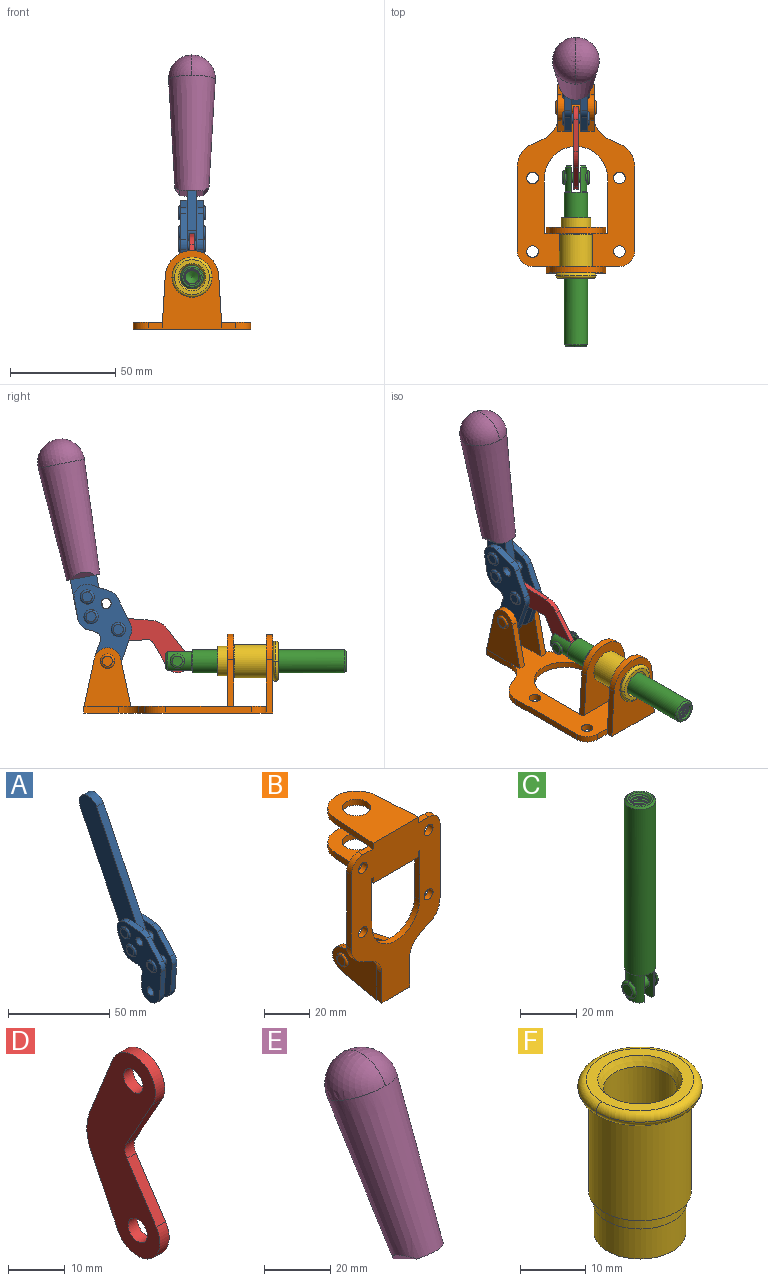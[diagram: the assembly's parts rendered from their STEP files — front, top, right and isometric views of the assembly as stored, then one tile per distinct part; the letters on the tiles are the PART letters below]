
ASSEMBLY  parts=6 mates=6
PART A: 59 faces, bbox 12.9x60.2x99.6 mm
  f0: torus R=2.39mm, axis (-1,0,0), area 14.9mm2, adj f20,f43,f51
  f1: torus R=2.39mm, axis (-1,0,0), area 14.9mm2, adj f19,f42,f51
  f2: torus R=2.39mm, axis (-1,0,0), area 14.9mm2, adj f18,f35,f51
  f3: torus R=2.39mm, axis (-1,0,0), area 14.9mm2, adj f14,f17,f23
  f4: torus R=2.39mm, axis (-1,0,0), area 14.9mm2, adj f13,f16,f23
  f5: torus R=2.39mm, axis (-1,0,0), area 14.9mm2, adj f12,f15,f23
  f6: cylinder r=2.39mm len=4.78mm, axis (1,0,0), area 46.5mm2, adj f48,f50,f51
  f7: cylinder r=2.39mm len=4.78mm, axis (1,0,0), area 46.5mm2, adj f50,f51
  f8: cylinder r=6.35mm len=12.68mm, axis (1,0,0), area 61.8mm2, adj f38,f39,f50,f51
  f9: cylinder r=2.39mm len=4.78mm, axis (-1,0,0), area 70.5mm2, adj f46,f50
  f10: cylinder r=2.39mm len=4.78mm, axis (-1,0,0), area 46.5mm2, adj f23,f45,f46
  f11: cylinder r=2.39mm len=4.78mm, axis (-1,0,0), area 46.5mm2, adj f23,f46
  f12: plane 4.78x4.78mm, normal (1,0,0), area 17.9mm2, adj f5,f15
  f13: plane 4.78x4.78mm, normal (1,0,0), area 17.9mm2, adj f4,f16
  f14: plane 4.78x4.78mm, normal (1,0,0), area 17.9mm2, adj f3,f17
  f15: torus R=2.39mm, axis (-1,0,0), area 14.9mm2, adj f5,f12,f23
  f16: torus R=2.39mm, axis (-1,0,0), area 14.9mm2, adj f4,f13,f23
  f17: torus R=2.39mm, axis (-1,0,0), area 14.9mm2, adj f3,f14,f23
  f18: plane 4.78x4.78mm, normal (-1,0,0), area 17.9mm2, adj f2,f35
  f19: plane 4.78x4.78mm, normal (-1,0,0), area 17.9mm2, adj f1,f42
  f20: plane 4.78x4.78mm, normal (-1,0,0), area 17.9mm2, adj f0,f43
  f21: plane 2.26x0.2mm, normal (1,0,0), area 0.2mm2, adj f31,f44
  f22: plane 2.26x0.2mm, normal (-1,0,0), area 0.2mm2, adj f41,f44
  f23: plane 39.37x30.77mm, normal (1,0,0), area 565.5mm2, adj f3,f4,f5,f10,f11,f15,f16,f17
  f24: cylinder r=6.1mm len=4.15mm, axis (-1,0,0), area 14.7mm2, adj f23,f25,f32,f46
  f25: plane 10.25x9.01mm, normal (0,-0.75,0.66), area 42.3mm2, adj f23,f24,f26,f46
  f26: cylinder r=6.35mm len=4.64mm, axis (-1,0,0), area 15.6mm2, adj f23,f25,f27,f46
  f27: plane 15.84x3.1mm, normal (0,-1,-0.07), area 49.2mm2, adj f23,f26,f28,f46
  f28: cylinder r=6.35mm len=12.68mm, axis (-1,0,0), area 61.8mm2, adj f23,f27,f29,f46
  f29: plane 8.11x3.1mm, normal (0,1,0.07), area 25.2mm2, adj f23,f28,f30,f46
  f30: cylinder r=3.05mm len=3.25mm, axis (-1,0,0), area 14.8mm2, adj f23,f29,f31,f46
  f31: plane 5.99x3.1mm, normal (0,0.07,-1), area 18.6mm2, adj f21,f23,f30,f44,f46
  f32: plane 9.5x3.1mm, normal (0,-0.07,1), area 29.5mm2, adj f23,f24,f33,f46,f47
  f33: cylinder r=6.1mm len=8.63mm, axis (-1,0,0), area 39.1mm2, adj f23,f32,f34,f47
  f34: plane 8.65x3.96mm, normal (0,0.91,-0.42), area 29.5mm2, adj f23,f33,f44,f47
  f35: torus R=2.39mm, axis (-1,0,0), area 14.9mm2, adj f2,f18,f51
  f36: plane 10.25x9.01mm, normal (0,-0.75,0.66), area 42.3mm2, adj f37,f49,f50,f51
  f37: cylinder r=6.35mm len=4.64mm, axis (1,0,0), area 15.6mm2, adj f36,f38,f50,f51
  f38: plane 15.84x3.1mm, normal (0,-1,-0.07), area 49.2mm2, adj f8,f37,f50,f51
  f39: plane 8.11x3.1mm, normal (0,1,0.07), area 25.2mm2, adj f8,f40,f50,f51
  f40: cylinder r=3.05mm len=3.25mm, axis (1,0,0), area 14.8mm2, adj f39,f41,f50,f51
  f41: plane 5.99x3.1mm, normal (0,0.07,-1), area 18.6mm2, adj f22,f40,f44,f50,f51
  f42: torus R=2.39mm, axis (-1,0,0), area 14.9mm2, adj f1,f19,f51
  f43: torus R=2.39mm, axis (-1,0,0), area 14.9mm2, adj f0,f20,f51
  f44: cylinder r=6.35mm len=12.12mm, axis (-1,0,0), area 128.9mm2, adj f21,f22,f23,f31,f34,f41,f46,f47
  f45: plane 2.65x1.35mm, normal (1,0,0), area 1mm2, adj f10,f55
  f46: plane 39.08x20.42mm, normal (-1,0,0), area 412.5mm2, adj f9,f10,f11,f24,f25,f26,f27,f28
  f47: plane 77.62x39.82mm, normal (1,0,0), area 850mm2, adj f32,f33,f34,f44,f53,f54,f55
  f48: plane 2.65x1.35mm, normal (-1,0,0), area 1mm2, adj f6,f55
  f49: cylinder r=6.1mm len=4.15mm, axis (1,0,0), area 14.7mm2, adj f36,f50,f51,f56
  f50: plane 39.08x20.42mm, normal (1,0,0), area 412.5mm2, adj f6,f7,f8,f9,f36,f37,f38,f39
  f51: plane 39.37x30.77mm, normal (-1,0,0), area 565.5mm2, adj f0,f1,f2,f6,f7,f8,f35,f36
  f52: plane 8.65x3.96mm, normal (0,0.91,-0.42), area 29.5mm2, adj f44,f51,f57,f58
  f53: plane 68.49x33.4mm, normal (0,0.9,-0.44), area 358.1mm2, adj f44,f47,f54,f58
  f54: cylinder r=6.35mm len=12.06mm, axis (1,0,0), area 93.7mm2, adj f47,f53,f55,f58
  f55: plane 68.49x33.4mm, normal (0,-0.9,0.44), area 358.1mm2, adj f44,f45,f46,f47,f48,f50,f54,f58
  f56: plane 9.5x3.1mm, normal (0,-0.07,1), area 29.5mm2, adj f49,f50,f51,f57,f58
  f57: cylinder r=6.1mm len=8.63mm, axis (1,0,0), area 39.1mm2, adj f51,f52,f56,f58
  f58: plane 77.62x39.82mm, normal (-1,0,0), area 850mm2, adj f44,f52,f53,f54,f55,f56,f57
PART B: 55 faces, bbox 55.7x37.4x89.8 mm
  f0: torus R=2.41mm, axis (-1,0,0), area 15mm2, adj f11,f15,f25
  f1: torus R=2.41mm, axis (-1,0,0), area 15mm2, adj f10,f12,f22
  f2: cylinder r=2.78mm len=5.56mm, axis (0,-1,0), area 54.2mm2, adj f30,f54
  f3: cylinder r=14.99mm len=29.97mm, axis (0,-1,0), area 145.9mm2, adj f30,f49,f53,f54
  f4: cylinder r=2.78mm len=5.56mm, axis (0,-1,0), area 54.2mm2, adj f30,f54
  f5: cylinder r=2.78mm len=5.56mm, axis (0,-1,0), area 54.2mm2, adj f30,f54
  f6: cylinder r=2.78mm len=5.56mm, axis (0,-1,0), area 54.2mm2, adj f30,f54
  f7: cylinder r=6.35mm len=12.7mm, axis (0,0,1), area 123.6mm2, adj f27,f51
  f8: cylinder r=6.35mm len=12.7mm, axis (0,0,-1), area 124.7mm2, adj f21,f35
  f9: cylinder r=2.41mm len=11.18mm, axis (-1,0,0), area 169.4mm2, adj f16,f19
  f10: plane 4.83x4.83mm, normal (1,0,0), area 18.3mm2, adj f1,f12
  f11: plane 4.83x4.83mm, normal (-1,0,0), area 18.3mm2, adj f0,f15
  f12: torus R=2.41mm, axis (-1,0,0), area 15mm2, adj f1,f10,f22
  f13: cylinder r=6.35mm len=12.41mm, axis (1,0,0), area 53.4mm2, adj f18,f19,f22,f23
  f14: cylinder r=6.35mm len=12.41mm, axis (-1,0,0), area 53.4mm2, adj f16,f17,f24,f25
  f15: torus R=2.41mm, axis (-1,0,0), area 15mm2, adj f0,f11,f25
  f16: plane 27.86x22.35mm, normal (1,0,0), area 425.4mm2, adj f9,f14,f17,f24,f30
  f17: plane 22.86x4.97mm, normal (0,0.21,0.98), area 72.5mm2, adj f14,f16,f25,f30
  f18: plane 22.86x4.97mm, normal (0,0.21,0.98), area 72.5mm2, adj f13,f19,f22,f30
  f19: plane 27.86x22.35mm, normal (-1,0,0), area 425.4mm2, adj f9,f13,f18,f23,f30
  f20: cylinder r=12.7mm len=25.35mm, axis (0,0,-1), area 119.8mm2, adj f21,f34,f35,f36
  f21: plane 34.21x28.07mm, normal (0,0,-1), area 702.4mm2, adj f8,f20,f30,f34,f36
  f22: plane 27.96x22.45mm, normal (1,0,0), area 407.2mm2, adj f1,f12,f13,f18,f23,f30,f42,f43
  f23: plane 22.86x4.97mm, normal (0,0.21,-0.98), area 72.5mm2, adj f13,f19,f22,f44
  f24: plane 22.86x4.97mm, normal (0,0.21,-0.98), area 72.5mm2, adj f14,f16,f25,f44
  f25: plane 27.86x22.35mm, normal (-1,0,0), area 407.1mm2, adj f0,f14,f15,f17,f24,f30,f45,f46
  f26: plane 3.1x0.95mm, normal (0,0,-1), area 2.7mm2, adj f30,f49,f50,f54
  f27: plane 34.21x28.07mm, normal (0,0,1), area 702.4mm2, adj f7,f28,f30,f50,f52
  f28: cylinder r=12.7mm len=25.35mm, axis (0,0,1), area 118.8mm2, adj f27,f50,f51,f52
  f29: plane 3.1x0.95mm, normal (0,0,-1), area 2.7mm2, adj f30,f52,f53,f54
  f30: plane 86.54x55.63mm, normal (0,1,0), area 2362.9mm2, adj f2,f3,f4,f5,f6,f16,f17,f18
  f31: plane 40.56x3.1mm, normal (-1,0,0), area 125.7mm2, adj f30,f32,f48,f54
  f32: cylinder r=7.11mm len=7.11mm, axis (0,-1,0), area 34.6mm2, adj f30,f31,f33,f54
  f33: plane 6.67x3.1mm, normal (0,0,1), area 20.4mm2, adj f30,f32,f34,f54
  f34: plane 25.39x3.13mm, normal (-1,0.06,0), area 79.5mm2, adj f20,f21,f33,f35,f54
  f35: plane 37.31x28.45mm, normal (0,0,1), area 789.9mm2, adj f8,f20,f34,f36,f54
  f36: plane 25.39x3.13mm, normal (1,0.06,0), area 79.5mm2, adj f20,f21,f35,f37,f54
  f37: plane 6.67x3.1mm, normal (0,0,1), area 20.4mm2, adj f30,f36,f38,f54
  f38: cylinder r=7.11mm len=7.11mm, axis (0,-1,0), area 34.6mm2, adj f30,f37,f39,f54
  f39: plane 40.56x3.1mm, normal (1,0,0), area 125.7mm2, adj f30,f38,f40,f54
  f40: cylinder r=11.18mm len=10.16mm, axis (0,-1,0), area 39.5mm2, adj f30,f39,f41,f54
  f41: plane 6.09x3.1mm, normal (0.42,0,-0.91), area 20.8mm2, adj f30,f40,f42,f54
  f42: cylinder r=11.18mm len=9.41mm, axis (0,-1,0), area 37.2mm2, adj f22,f30,f41,f43,f54
  f43: plane 16.5x3.1mm, normal (1,0,0), area 51.1mm2, adj f22,f42,f44,f54
  f44: plane 17.37x3.1mm, normal (0,0,-1), area 53.8mm2, adj f23,f24,f30,f43,f45,f54
  f45: plane 16.5x3.1mm, normal (-1,0,0), area 51.1mm2, adj f25,f44,f46,f54
  f46: cylinder r=11.18mm len=9.41mm, axis (0,-1,0), area 37.2mm2, adj f25,f30,f45,f47,f54
  f47: plane 6.09x3.1mm, normal (-0.42,0,-0.91), area 20.8mm2, adj f30,f46,f48,f54
  f48: cylinder r=11.18mm len=10.16mm, axis (0,-1,0), area 39.5mm2, adj f30,f31,f47,f54
  f49: plane 26.54x3.1mm, normal (-1,0,0), area 82.3mm2, adj f3,f26,f30,f54
  f50: plane 25.39x3.1mm, normal (1,0.06,0), area 78.8mm2, adj f26,f27,f28,f51,f54
  f51: plane 37.31x28.45mm, normal (0,0,-1), area 789.9mm2, adj f7,f28,f50,f52,f54
  f52: plane 25.39x3.1mm, normal (-1,0.06,0), area 78.8mm2, adj f27,f28,f29,f51,f54
  f53: plane 26.54x3.1mm, normal (1,0,0), area 82.3mm2, adj f3,f29,f30,f54
  f54: plane 89.66x55.63mm, normal (0,-1,0), area 2678.5mm2, adj f2,f3,f4,f5,f6,f26,f29,f31
PART C: 48 faces, bbox 12.6x11.1x86.1 mm
  f0: torus R=2.41mm, axis (-1,0,0), area 15mm2, adj f30,f32,f34
  f1: torus R=2.41mm, axis (-1,0,0), area 15mm2, adj f29,f31,f33
  f2: cylinder r=5.54mm len=72.39mm, axis (0,0,1), area 2518.5mm2, adj f3,f4,f42,f43
  f3: cone r=5.54mm half-angle=45deg, axis (0,0,1), area 7.6mm2, adj f2,f5,f41
  f4: cone r=5.54mm half-angle=45deg, axis (0,0,-1), area 34.9mm2, adj f2,f39
  f5: cylinder r=5.08mm len=11.48mm, axis (0,0,1), area 108.3mm2, adj f3,f7,f8,f41
  f6: cylinder r=2.41mm len=4.83mm, axis (-1,0,0), area 71.2mm2, adj f40,f41
  f7: cylinder r=2.41mm len=4.83mm, axis (-1,0,0), area 7.6mm2, adj f5,f34
  f8: cone r=5.08mm half-angle=45deg, axis (0,0,1), area 10.6mm2, adj f5,f37,f41
  f9: cone r=3.98mm half-angle=45deg, axis (0,0,1), area 17.6mm2, adj f27,f39,f45,f46,f47
  f10: cylinder r=2.41mm len=4.83mm, axis (-1,0,0), area 7.6mm2, adj f33,f38
  f11: cylinder r=3.2mm len=6.4mm, axis (0,0,1), area 78.4mm2, adj f12,f28,f44,f45,f47
  f12: cylinder r=3.2mm len=6.4mm, axis (0,0,1), area 10.5mm2, adj f11,f13,f45,f47
  f13: cylinder r=3.2mm len=6.4mm, axis (0,0,1), area 10.5mm2, adj f12,f14,f45,f47
  f14: cylinder r=3.2mm len=6.4mm, axis (0,0,1), area 10.5mm2, adj f13,f15,f45,f47
  f15: cylinder r=3.2mm len=6.4mm, axis (0,0,1), area 10.5mm2, adj f14,f16,f45,f47
  f16: cylinder r=3.2mm len=6.4mm, axis (0,0,1), area 10.5mm2, adj f15,f17,f45,f47
  f17: cylinder r=3.2mm len=6.4mm, axis (0,0,1), area 10.5mm2, adj f16,f18,f45,f47
  f18: cylinder r=3.2mm len=6.4mm, axis (0,0,1), area 10.5mm2, adj f17,f19,f45,f47
  f19: cylinder r=3.2mm len=6.4mm, axis (0,0,1), area 10.5mm2, adj f18,f20,f45,f47
  f20: cylinder r=3.2mm len=6.4mm, axis (0,0,1), area 10.5mm2, adj f19,f21,f45,f47
  f21: cylinder r=3.2mm len=6.4mm, axis (0,0,1), area 10.5mm2, adj f20,f22,f45,f47
  f22: cylinder r=3.2mm len=6.4mm, axis (0,0,1), area 10.5mm2, adj f21,f23,f45,f47
  f23: cylinder r=3.2mm len=6.4mm, axis (0,0,1), area 10.5mm2, adj f22,f24,f45,f47
  f24: cylinder r=3.2mm len=6.4mm, axis (0,0,1), area 10.5mm2, adj f23,f25,f45,f47
  f25: cylinder r=3.2mm len=6.4mm, axis (0,0,1), area 10.5mm2, adj f24,f26,f45,f47
  f26: cylinder r=3.2mm len=6.4mm, axis (0,0,1), area 10.5mm2, adj f25,f27,f45,f47
  f27: cylinder r=3.2mm len=6.4mm, axis (0,0,1), area 7.4mm2, adj f9,f26,f45,f47
  f28: cone r=3.2mm half-angle=60deg, axis (0,0,1), area 37.2mm2, adj f11
  f29: plane 4.83x4.83mm, normal (-1,0,0), area 18.3mm2, adj f1,f31
  f30: plane 4.83x4.83mm, normal (1,0,0), area 18.3mm2, adj f0,f32
  f31: torus R=2.41mm, axis (-1,0,0), area 15mm2, adj f1,f29,f33
  f32: torus R=2.41mm, axis (-1,0,0), area 15mm2, adj f0,f30,f34
  f33: plane 6.83x6.83mm, normal (1,0,0), area 18.3mm2, adj f1,f10,f31
  f34: plane 6.83x6.83mm, normal (-1,0,0), area 18.3mm2, adj f0,f7,f32
  f35: cone r=5.08mm half-angle=45deg, axis (0,0,1), area 10.6mm2, adj f36,f38,f40
  f36: plane 7.25x1.97mm, normal (0,0,-1), area 10mm2, adj f35,f40
  f37: plane 7.25x1.97mm, normal (0,0,-1), area 10mm2, adj f8,f41
  f38: cylinder r=5.08mm len=11.48mm, axis (0,0,1), area 108.3mm2, adj f10,f35,f40,f42
  f39: plane 9.55x9.55mm, normal (0,0,1), area 22mm2, adj f4,f9
  f40: plane 12.76x10.09mm, normal (1,0,0), area 95.7mm2, adj f6,f35,f36,f38,f42,f43
  f41: plane 12.76x10.09mm, normal (-1,0,0), area 95.7mm2, adj f3,f5,f6,f8,f37,f43
  f42: cone r=5.54mm half-angle=45deg, axis (0,0,1), area 7.6mm2, adj f2,f38,f40
  f43: plane 11.07x4.7mm, normal (0,0,-1), area 50.4mm2, adj f2,f40,f41
  f44: plane 0.89x0.62mm, normal (-1,0,0), area 0.3mm2, adj f11,f45,f46,f47
  f45: bspline ~24.8x7.63mm, area 266.6mm2, adj f9,f11,f12,f13,f14,f15,f16,f17
  f46: bspline ~24.87x7.63mm, area 73.6mm2, adj f9,f44,f45,f47
  f47: bspline ~24.98x7.63mm, area 272.5mm2, adj f9,f11,f12,f13,f14,f15,f16,f17
PART D: 12 faces, bbox 2.3x18.2x42.8 mm
  f0: cylinder r=2.4mm len=4.8mm, axis (1,0,0), area 34.9mm2, adj f4,f11
  f1: cylinder r=10.41mm len=8.47mm, axis (1,0,0), area 20.2mm2, adj f4,f9,f10,f11
  f2: cylinder r=3.05mm len=3.16mm, axis (1,0,0), area 7.7mm2, adj f4,f6,f7,f11
  f3: cylinder r=2.4mm len=4.8mm, axis (1,0,0), area 34.9mm2, adj f4,f11
  f4: plane 42.81x18.23mm, normal (-1,0,0), area 414.1mm2, adj f0,f1,f2,f3,f5,f6,f7,f8
  f5: cylinder r=5.54mm len=10.67mm, axis (1,0,0), area 41.8mm2, adj f4,f6,f10,f11
  f6: plane 11.66x6.53mm, normal (0,-0.87,-0.49), area 30.9mm2, adj f2,f4,f5,f11
  f7: plane 11.17x7.33mm, normal (0,-0.84,0.55), area 30.9mm2, adj f2,f4,f8,f11
  f8: cylinder r=5.54mm len=10.51mm, axis (1,0,0), area 41.8mm2, adj f4,f7,f9,f11
  f9: plane 13.67x6.67mm, normal (0,0.9,-0.44), area 35.1mm2, adj f1,f4,f8,f11
  f10: plane 14.1x5.7mm, normal (0,0.93,0.37), area 35.1mm2, adj f1,f4,f5,f11
  f11: plane 42.81x18.23mm, normal (1,0,0), area 414.1mm2, adj f0,f1,f2,f3,f5,f6,f7,f8
PART E: 11 faces, bbox 22.3x42.6x64.5 mm
  f0: sphere r=11.13mm, area 411.4mm2, adj f1,f8
  f1: cone r=11.11mm half-angle=3.3deg, axis (0,0.44,0.9), area 3251.8mm2, adj f0,f7,f8,f9,f10
  f2: cylinder r=6.16mm len=11.7mm, axis (1,0,0), area 89.5mm2, adj f3,f4,f5,f6
  f3: plane 60.23x36.75mm, normal (-1,0,0), area 763.6mm2, adj f2,f4,f6,f10
  f4: plane 51.37x25.05mm, normal (0,0.9,-0.44), area 264.2mm2, adj f2,f3,f5,f10
  f5: plane 60.23x36.75mm, normal (1,0,0), area 763.6mm2, adj f2,f4,f6,f10
  f6: plane 51.37x25.05mm, normal (0,-0.9,0.44), area 264.2mm2, adj f2,f3,f5,f10
  f7: plane 9.95x5.95mm, normal (0.71,-0.31,-0.64), area 25.8mm2, adj f1,f10
  f8: sphere r=11.13mm, area 411.4mm2, adj f0,f1
  f9: plane 9.95x5.95mm, normal (-0.71,-0.31,-0.64), area 25.8mm2, adj f1,f10
  f10: plane 14.27x11.38mm, normal (0,-0.44,-0.9), area 106.7mm2, adj f1,f3,f4,f5,f6,f7,f9
PART F: 15 faces, bbox 20.6x20.6x28.7 mm
  f0: torus R=8.26mm, axis (0,0,1), area 56.8mm2, adj f1,f10,f12
  f1: torus R=8.26mm, axis (0,0,1), area 56.8mm2, adj f0,f6,f13
  f2: cylinder r=5.59mm len=25.91mm, axis (0,0,1), area 909.6mm2, adj f3,f4
  f3: cone r=6.86mm half-angle=45deg, axis (0,0,-1), area 70.2mm2, adj f2,f14
  f4: cone r=6.47mm half-angle=30deg, axis (0,0,1), area 66.7mm2, adj f2,f13
  f5: cylinder r=7.04mm len=14.07mm, axis (0,0,1), area 252.6mm2, adj f11,f14
  f6: torus R=8.26mm, axis (0,0,1), area 56.8mm2, adj f1,f12,f13
  f7: cylinder r=7.16mm len=14.33mm, axis (0,0,1), area 91.5mm2, adj f9,f11
  f8: cylinder r=7.86mm len=18.42mm, axis (0,0,1), area 909.6mm2, adj f9,f10
  f9: plane 15.72x15.72mm, normal (0,0,-1), area 33mm2, adj f7,f8
  f10: plane 16.51x16.51mm, normal (0,0,-1), area 19.9mm2, adj f0,f8,f12
  f11: plane 14.33x14.33mm, normal (0,0,-1), area 5.7mm2, adj f5,f7
  f12: torus R=8.26mm, axis (0,0,1), area 56.8mm2, adj f0,f6,f10
  f13: plane 16.51x16.51mm, normal (0,0,1), area 82.7mm2, adj f1,f4,f6
  f14: plane 14.07x14.07mm, normal (0,0,-1), area 7.8mm2, adj f3,f5
PLACE A rot(axis=(1,0,0),15deg) t=(0,9.15,49.24)mm
PLACE B rot(axis=(1,0,0),90deg) t=(0,9.14,0)mm fixed
PLACE C rot(axis=(1,0,0),90deg) t=(0,23.56,0)mm
PLACE D rot(axis=(0,-0.53,-0.85),180deg) t=(0,33.05,10.71)mm
PLACE E rot(axis=(1,0,0),15deg) t=(-0.04,9.15,49.24)mm
PLACE F rot(axis=(1,0,0),90deg) t=(0,9.14,0)mm
MATE revolute D.f3 <-> C.f6  axis (-1,0,0) through (0,8.09,24.61)mm
MATE revolute A.f7 <-> B.f0  axis (-1,0,0) through (0,41.23,24.61)mm
MATE fastened F.f0 <-> B.f7  axis (0,1,0) through (0,-37.25,24.61)mm
MATE slider C.f2 <-> B.f7  axis (0,-1,0) through (0,-35.22,24.61)mm
MATE fastened E.f2 <-> A.f54  axis (1,0,0) through (-2.35,63.6,120.54)mm
MATE revolute D.f5 <-> A.f4  axis (-1,0,0) through (0,36.06,39.62)mm
